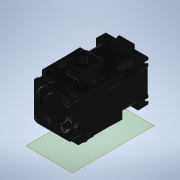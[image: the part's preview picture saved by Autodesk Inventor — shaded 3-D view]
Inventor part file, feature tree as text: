
AUTODESK INVENTOR PART (.ipt)
format: ipt  version: 2020.2 (Build 242310000, 310)  size: 3,910,656 bytes
history: native  units: mm (DEFAULTED — no unit token found)
features: other x2, plane x2
ambient origin geometry x8: Origin, YZ Plane, XZ Plane, XY Plane, X Axis, Y Axis, Z Axis, Center Point
feature tree (4):
  other  "HEMERA-MODEL-1-(3)"
  plane  "Work Plane1"
  plane  "Work Plane2"
  other  "MeshFeature1"
